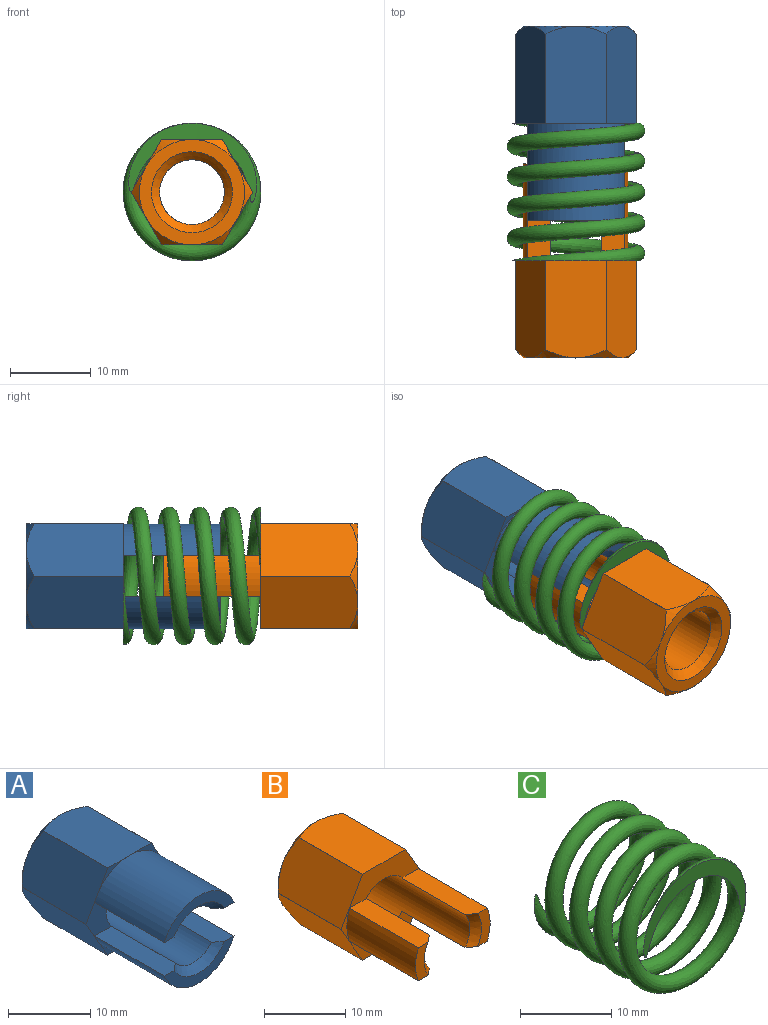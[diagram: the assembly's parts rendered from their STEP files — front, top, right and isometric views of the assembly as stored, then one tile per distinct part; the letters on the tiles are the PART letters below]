
ASSEMBLY  parts=3 mates=3
PART A: 37 faces, bbox 15.1x24.1x15.1 mm
  f0: cylinder r=7.5mm len=11mm, axis (0,1,0), area 0.2mm2, adj f9,f14,f23,f34
  f1: cylinder r=7.5mm len=11mm, axis (0,1,0), area 0.2mm2, adj f13,f14,f15,f30
  f2: cylinder r=7.5mm len=11mm, axis (0,1,0), area 0.2mm2, adj f12,f13,f16,f33
  f3: cylinder r=7.5mm len=11mm, axis (0,1,0), area 0.2mm2, adj f11,f12,f17,f32
  f4: cylinder r=7.5mm len=11mm, axis (0,1,0), area 0.2mm2, adj f10,f11,f18,f29
  f5: cylinder r=4mm len=22mm, axis (0,1,0), area 434.1mm2, adj f8,f22,f24,f25,f26,f29,f30,f35
  f6: cylinder r=7.5mm len=11mm, axis (0,1,0), area 0.2mm2, adj f9,f10,f19,f31
  f7: plane 12x4mm, normal (0,-1,0), area 19.3mm2, adj f8,f25,f27,f35
  f8: cone r=4mm half-angle=45deg, axis (0,-1,0), area 12.4mm2, adj f5,f7,f25,f35
  f9: plane 12.01x7.49mm, normal (0,0,-1), area 87.2mm2, adj f0,f6,f19,f23,f31,f34
  f10: plane 12x6.49mm, normal (0.87,0,-0.5), area 87.2mm2, adj f4,f6,f18,f19,f29,f31
  f11: plane 12x6.49mm, normal (0.87,0,0.5), area 87.2mm2, adj f3,f4,f17,f18,f29,f32
  f12: plane 12.01x7.49mm, normal (0,0,1), area 87.2mm2, adj f2,f3,f16,f17,f32,f33
  f13: plane 12x6.49mm, normal (-0.87,0,0.5), area 87.2mm2, adj f1,f2,f15,f16,f30,f33
  f14: plane 12x6.49mm, normal (-0.87,0,-0.5), area 87.2mm2, adj f0,f1,f15,f23,f30,f34
  f15: cone r=7.5mm half-angle=45deg, axis (0,-1,0), area 3.2mm2, adj f1,f13,f14,f21
  f16: cone r=7.5mm half-angle=45deg, axis (0,-1,0), area 3.2mm2, adj f2,f12,f13,f21
  f17: cone r=7.5mm half-angle=45deg, axis (0,-1,0), area 3.2mm2, adj f3,f11,f12,f21
  f18: cone r=7.5mm half-angle=45deg, axis (0,-1,0), area 3.2mm2, adj f4,f10,f11,f21
  f19: cone r=7.5mm half-angle=45deg, axis (0,-1,0), area 3.2mm2, adj f6,f9,f10,f21
  f20: plane 12x4mm, normal (0,-1,0), area 19.3mm2, adj f24,f26,f28,f36
  f21: plane 13x13mm, normal (0,1,0), area 54.2mm2, adj f15,f16,f17,f18,f19,f22,f23
  f22: cone r=5mm half-angle=45deg, axis (0,1,0), area 40mm2, adj f5,f21
  f23: cone r=7.5mm half-angle=45deg, axis (0,-1,0), area 3.2mm2, adj f0,f9,f14,f21
  f24: cone r=4mm half-angle=45deg, axis (0,-1,0), area 12.4mm2, adj f5,f20,f26,f36
  f25: plane 12.09x2.96mm, normal (0,0,-1), area 33.9mm2, adj f5,f7,f8,f27,f30
  f26: plane 12.09x2.96mm, normal (0,0,1), area 33.9mm2, adj f5,f20,f24,f28,f30
  f27: cylinder r=6.5mm len=12mm, axis (0,-1,0), area 183.5mm2, adj f7,f25,f29,f30,f32,f33,f35
  f28: cylinder r=6.5mm len=12mm, axis (0,-1,0), area 183.5mm2, adj f20,f26,f29,f30,f31,f34,f36
  f29: plane 6.5x4.38mm, normal (0,-1,0), area 15.3mm2, adj f4,f5,f10,f11,f27,f28,f35,f36
  f30: plane 6.5x4.38mm, normal (0,-1,0), area 15.3mm2, adj f1,f5,f13,f14,f25,f26,f27,f28
  f31: plane 5.63x3.25mm, normal (0,-1,0), area 2.3mm2, adj f6,f9,f10,f28
  f32: plane 5.63x3.25mm, normal (0,-1,0), area 2.3mm2, adj f3,f11,f12,f27
  f33: plane 5.63x3.25mm, normal (0,-1,0), area 2.3mm2, adj f2,f12,f13,f27
  f34: plane 5.63x3.25mm, normal (0,-1,0), area 2.3mm2, adj f0,f9,f14,f28
  f35: plane 12.09x2.96mm, normal (0,0,-1), area 33.9mm2, adj f5,f7,f8,f27,f29
  f36: plane 12.09x2.96mm, normal (0,0,1), area 33.9mm2, adj f5,f20,f24,f28,f29
PART B: 32 faces, bbox 15.1x24.1x15.1 mm
  f0: cylinder r=7.5mm len=11mm, axis (0,1,0), area 0.2mm2, adj f11,f16,f24,f27
  f1: cylinder r=7.5mm len=11mm, axis (0,1,0), area 0.2mm2, adj f15,f16,f17,f27
  f2: cylinder r=7.5mm len=11mm, axis (0,1,0), area 0.2mm2, adj f14,f15,f18,f27
  f3: cylinder r=7.5mm len=11mm, axis (0,1,0), area 0.2mm2, adj f13,f14,f19,f27
  f4: cylinder r=7.5mm len=11mm, axis (0,1,0), area 0.2mm2, adj f12,f13,f20,f27
  f5: cylinder r=4mm len=22mm, axis (0,1,0), area 395.3mm2, adj f9,f10,f23,f25,f26,f27,f28,f30
  f6: cylinder r=7.5mm len=11mm, axis (0,1,0), area 0.2mm2, adj f11,f12,f21,f27
  f7: plane 5x2.17mm, normal (0,-1,0), area 7.8mm2, adj f9,f25,f26,f31
  f8: plane 5x2.17mm, normal (0,-1,0), area 7.8mm2, adj f10,f28,f29,f30
  f9: cone r=4mm half-angle=45deg, axis (0,-1,0), area 7.6mm2, adj f5,f7,f25,f26
  f10: cone r=4mm half-angle=45deg, axis (0,-1,0), area 7.6mm2, adj f5,f8,f28,f30
  f11: plane 12.01x7.49mm, normal (0,0,-1), area 87.2mm2, adj f0,f6,f21,f24,f27
  f12: plane 12x6.49mm, normal (0.87,0,-0.5), area 87.2mm2, adj f4,f6,f20,f21,f27
  f13: plane 12x6.49mm, normal (0.87,0,0.5), area 87.2mm2, adj f3,f4,f19,f20,f27
  f14: plane 12.01x7.49mm, normal (0,0,1), area 87.2mm2, adj f2,f3,f18,f19,f27
  f15: plane 12x6.49mm, normal (-0.87,0,0.5), area 87.2mm2, adj f1,f2,f17,f18,f27
  f16: plane 12x6.49mm, normal (-0.87,0,-0.5), area 87.2mm2, adj f0,f1,f17,f24,f27
  f17: cone r=7.5mm half-angle=45deg, axis (0,-1,0), area 3.2mm2, adj f1,f15,f16,f22
  f18: cone r=7.5mm half-angle=45deg, axis (0,-1,0), area 3.2mm2, adj f2,f14,f15,f22
  f19: cone r=7.5mm half-angle=45deg, axis (0,-1,0), area 3.2mm2, adj f3,f13,f14,f22
  f20: cone r=7.5mm half-angle=45deg, axis (0,-1,0), area 3.2mm2, adj f4,f12,f13,f22
  f21: cone r=7.5mm half-angle=45deg, axis (0,-1,0), area 3.2mm2, adj f6,f11,f12,f22
  f22: plane 13x13mm, normal (0,1,0), area 54.2mm2, adj f17,f18,f19,f20,f21,f23,f24
  f23: cone r=5mm half-angle=45deg, axis (0,1,0), area 40mm2, adj f5,f22
  f24: cone r=7.5mm half-angle=45deg, axis (0,-1,0), area 3.2mm2, adj f0,f11,f16,f22
  f25: plane 12.09x2.96mm, normal (0,0,1), area 33.9mm2, adj f5,f7,f9,f27,f31
  f26: plane 12.09x2.96mm, normal (0,0,-1), area 33.9mm2, adj f5,f7,f9,f27,f31
  f27: plane 15x13mm, normal (0,-1,0), area 69.9mm2, adj f0,f1,f2,f3,f4,f5,f6,f11
  f28: plane 12.09x2.96mm, normal (0,0,1), area 33.9mm2, adj f5,f8,f10,f27,f29
  f29: cylinder r=6.5mm len=12mm, axis (0,-1,0), area 61.6mm2, adj f8,f27,f28,f30
  f30: plane 12.09x2.96mm, normal (0,0,-1), area 33.9mm2, adj f5,f8,f10,f27,f29
  f31: cylinder r=6.5mm len=12mm, axis (0,-1,0), area 61.6mm2, adj f7,f25,f26,f27
PART C: 3 faces, bbox 17.5x21.6x17.6 mm
  f0: bspline ~20.98x16.97mm, area 1324.7mm2, adj f1,f2
  f1: plane 15.82x9.81mm, normal (0,1,0), area 39.1mm2, adj f0
  f2: plane 16.4x10.39mm, normal (0,-1,0), area 37.2mm2, adj f0
PLACE A t=(-38.48,13.4,-145.79)mm fixed
PLACE B rot(axis=(1,0,0),180deg) t=(-38.48,-27.6,178.26)mm
PLACE C t=(-103.2,2.4,-56.23)mm
MATE planar B.f27 <-> C.f2  axis (0,1,0) through (-7.52,-15.6,6.99)mm
MATE fastened A.f0 <-> C.f1  axis (0,-1,0) through (-1.89,1.4,3.74)mm
MATE slider A.f0 <-> B.f0  axis (0,-1,0) through (-1.89,-4.6,3.74)mm
